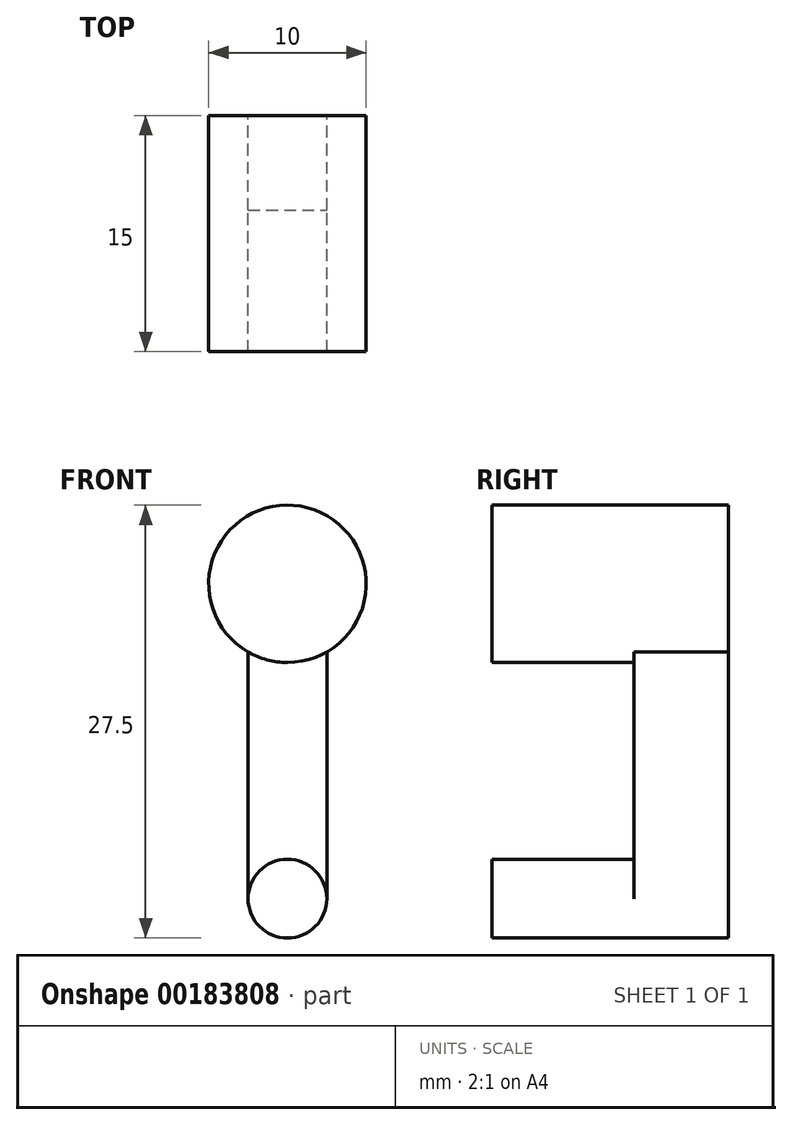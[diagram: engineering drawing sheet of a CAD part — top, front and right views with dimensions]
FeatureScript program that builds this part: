
annotation { "Feature Type Name" : "Feature", "Feature Type Description" : "" }
export const myFeature = defineFeature(function(context is Context, id is Id, definition is map)
    precondition{}
    {
        {
            var Q0;
            Q0=qCreatedBy(makeId("Front.planeOp"),FACE);
            var sketch = newSketch(context, id + "F0", { "sketchPlane" : qUnion([Q0])});
            skLineSegment(sketch, "E0.bottom", {"start": v(0, 0) * mm, "end": v(5, 0) * mm});
            skLineSegment(sketch, "E0.top", {"start": v(0, 20) * mm, "end": v(5, 20) * mm});
            skLineSegment(sketch, "E0.left", {"start": v(0, 0) * mm, "end": v(0, 20) * mm});
            skLineSegment(sketch, "E0.right", {"start": v(5, 0) * mm, "end": v(5, 20) * mm});
            skSolve(sketch);
        }
        {
            var Q0;
            Q0=makeQuery(id+"F0.imprint","IMPRINT",FACE,{"disambiguationData":[TD([[makeQuery(id+"F0.imprint","IMPRINT",EDGE,{"derivedFrom":sQuery(id+"F0.wireOp",EDGE,"E0.bottom")}),1.0]])]});
            extrude(context, id + "F1", {"entities" : qUnion([Q0]), "depth" : 6 * mm});
        }
        {
            var Q0;
            Q0=qCreatedBy(makeId("Front.planeOp"),FACE);
            var sketch = newSketch(context, id + "F2", { "sketchPlane" : qUnion([Q0])});
            skCircle(sketch, "E1", {"center": v(2.5, 0) * mm, "radius": 2.5 * mm});
            skCircle(sketch, "E2", {"center": v(2.5, 20) * mm, "radius": 5 * mm});
            skSolve(sketch);
        }
        {
            var Q0;
            Q0=makeQuery(id+"F2.imprint","IMPRINT",FACE,{"disambiguationData":[TD([[makeQuery(id+"F2.imprint","IMPRINT",EDGE,{"derivedFrom":sQuery(id+"F2.wireOp",EDGE,"E2")}),1.0]])]});
            var Q1;
            Q1=makeQuery(id+"F2.imprint","IMPRINT",FACE,{"disambiguationData":[TD([[makeQuery(id+"F2.imprint","IMPRINT",EDGE,{"derivedFrom":sQuery(id+"F2.wireOp",EDGE,"E1")}),1.0]])]});
            extrude(context, id + "F3", {"entities" : qUnion([Q0, Q1]), "operationType" : NewBodyOperationType.ADD, "depth" : 15 * mm});
        }
    });
